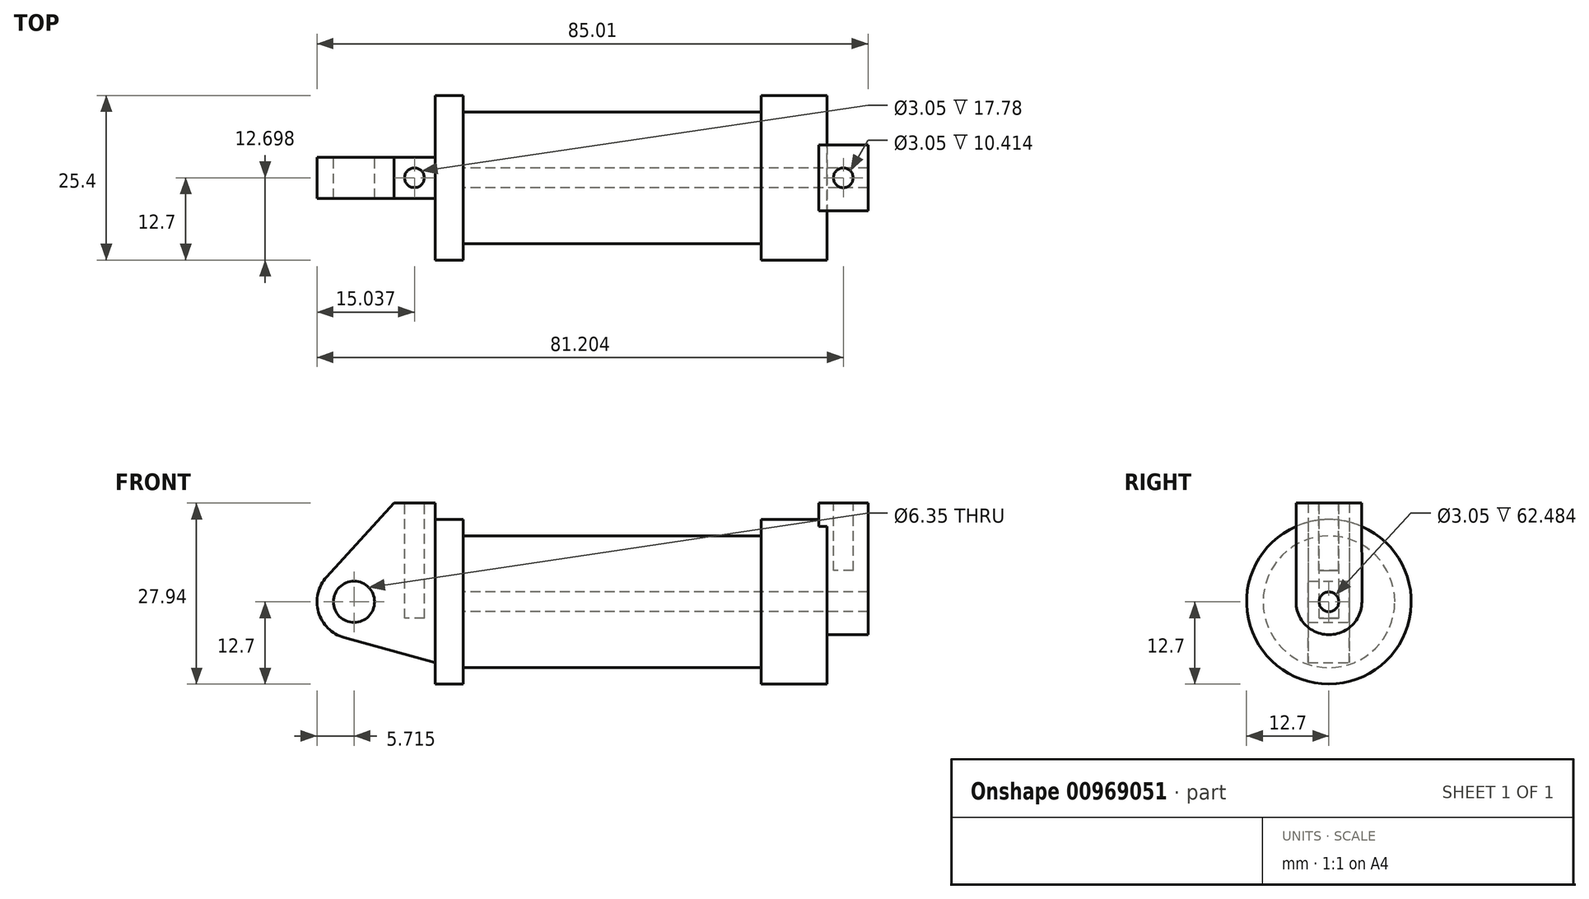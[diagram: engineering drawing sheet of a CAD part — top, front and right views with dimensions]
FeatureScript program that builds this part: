
annotation { "Feature Type Name" : "Feature", "Feature Type Description" : "" }
export const myFeature = defineFeature(function(context is Context, id is Id, definition is map)
    precondition{}
    {
        {
            var Q0;
            Q0=qCreatedBy(makeId("Front.planeOp"),FACE);
            var sketch = newSketch(context, id + "F0", { "sketchPlane" : qUnion([Q0])});
            skLineSegment(sketch, "E0", {"start": v(0, 0) * mm, "end": v(0, 12.7) * mm});
            skLineSegment(sketch, "E1", {"start": v(0, 12.7) * mm, "end": v(10.16, 12.7) * mm});
            skLineSegment(sketch, "E2", {"start": v(10.16, 12.7) * mm, "end": v(10.16, 10.16) * mm});
            skLineSegment(sketch, "E3", {"start": v(10.16, 10.16) * mm, "end": v(56.13, 10.16) * mm});
            skLineSegment(sketch, "E4", {"start": v(56.13, 10.16) * mm, "end": v(56.13, 12.7) * mm});
            skLineSegment(sketch, "E5", {"start": v(56.13, 12.7) * mm, "end": v(66.3, 12.7) * mm});
            skLineSegment(sketch, "E6", {"start": v(66.3, 12.7) * mm, "end": v(66.3, 0) * mm});
            skLineSegment(sketch, "E7", {"start": v(66.3, 0) * mm, "end": v(0, 0) * mm});
            skLineSegment(sketch, "E8", {"start": v(5.84, 15.24) * mm, "end": v(-0.5, 15.24) * mm});
            skLineSegment(sketch, "E9", {"start": v(-0.5, 15.24) * mm, "end": v(-10.88, 3.85) * mm});
            skLineSegment(sketch, "E10", {"start": v(0, 0) * mm, "end": v(-6.65, 0) * mm});
            skCircle(sketch, "E11", {"center": v(-6.65, 0) * mm, "radius": 5.72 * mm});
            skCircle(sketch, "E12", {"center": v(-6.65, 0) * mm, "radius": 3.18 * mm});
            skLineSegment(sketch, "E13", {"start": v(5.84, 15.24) * mm, "end": v(5.84, -9.4) * mm});
            skLineSegment(sketch, "E14", {"start": v(5.84, -9.4) * mm, "end": v(-8.18, -5.5) * mm});
            skSolve(sketch);
        }
        {
            var Q0;
            {var subQ0=sQuery(id+"F0.wireOp",EDGE,"E2");Q0=makeQuery(id+"F0.imprint","IMPRINT",FACE,{"disambiguationData":[TD([[makeQuery(id+"F0.imprint","IMPRINT",EDGE,{"derivedFrom":subQ0}),-1.0]])]});}
            var Q1;
            Q1=sQuery(id+"F0.wireOp",EDGE,"E10");
            revolve(context, id + "F1", {"surfaceOperationType" : NewSurfaceOperationType.NEW, "entities" : qUnion([Q0]), "axis" : qUnion([Q1]), "revolveType" : RevolveType.FULL});
        }
        {
            var Q0;
            {var subQ0=sQuery(id+"F0.wireOp",EDGE,"E14");Q0=makeQuery(id+"F0.imprint","IMPRINT",FACE,{"disambiguationData":[TD([[makeQuery(id+"F0.imprint","IMPRINT",EDGE,{"derivedFrom":subQ0}),-1.0]])]});}
            var Q1;
            {var subQ1=sQuery(id+"F0.wireOp",EDGE,"E0");Q1=makeQuery(id+"F0.imprint","IMPRINT",FACE,{"disambiguationData":[TD([[makeQuery(id+"F0.imprint","IMPRINT",EDGE,{"derivedFrom":subQ1}),1.0]])]});}
            var Q2;
            {var subQ5=sQuery(id+"F0.wireOp",EDGE,"E12");Q2=makeQuery(id+"F0.imprint","IMPRINT",FACE,{"disambiguationData":[TD([[makeQuery(id+"F0.imprint","IMPRINT",EDGE,{"derivedFrom":subQ5}),-1.0]])]});}
            var Q3;
            {var subQ0=sQuery(id+"F0.wireOp",EDGE,"E0");Q3=makeQuery(id+"F0.imprint","IMPRINT",FACE,{"disambiguationData":[TD([[makeQuery(id+"F0.imprint","IMPRINT",EDGE,{"derivedFrom":subQ0}),-1.0]])]});}
            extrude(context, id + "F2", {"entities" : qUnion([Q0, Q1, Q2, Q3]), "operationType" : NewBodyOperationType.ADD, "depth" : 3.17 * mm, "offsetDistance" : 25.4 * mm, "hasSecondDirection" : true, "secondDirectionOppositeDirection" : true, "secondDirectionDepth" : 3.17 * mm});
        }
        {
            var Q0;
            Q0=makeQuery(id+"F1.opRevolve","SWEPT_FACE",FACE,{"disambiguationData":[OSD([sQuery(id+"F0.wireOp",EDGE,"E6")])]});
            var sketch = newSketch(context, id + "F3", { "sketchPlane" : qUnion([Q0])});
            skCircle(sketch, "E15", {"center": v(0, 0) * mm, "radius": 1.52 * mm});
            skCircle(sketch, "E16", {"center": v(0, 0) * mm, "radius": 5.08 * mm});
            skLineSegment(sketch, "E17", {"start": v(-0.02, 15.24) * mm, "end": v(5.08, 15.24) * mm});
            skLineSegment(sketch, "E18", {"start": v(-0.02, 15.24) * mm, "end": v(-5.08, 15.24) * mm});
            skLineSegment(sketch, "E19", {"start": v(-5.08, 15.24) * mm, "end": v(-5.08, 0) * mm});
            skLineSegment(sketch, "E20", {"start": v(5.08, 15.24) * mm, "end": v(5.08, 0) * mm});
            skSolve(sketch);
        }
        {
            var Q0;
            {var subQ1=sQuery(id+"F3.wireOp",EDGE,"E17");Q0=makeQuery(id+"F3.imprint","IMPRINT",FACE,{"disambiguationData":[TD([[makeQuery(id+"F3.imprint","IMPRINT",EDGE,{"derivedFrom":subQ1}),-1.0]])]});}
            var Q1;
            {var subQ0=sQuery(id+"F3.wireOp",EDGE,"E19");var subQ1=sQuery(id+"F3.wireOp",EDGE,"E16");var subQ2=makeQuery(id+"F3.imprint","INTERSECT",VERTEX,{"derivedFrom":[subQ1,subQ0]});Q1=makeQuery(id+"F3.imprint","IMPRINT",FACE,{"disambiguationData":[TD([[makeQuery(id+"F3.imprint","IMPRINT",EDGE,{"disambiguationData":[TD([[subQ2,1.0]])],"derivedFrom":subQ1}),-1.0]])]});}
            var Q2;
            Q2=makeQuery(id+"F3.imprint","IMPRINT",FACE,{"disambiguationData":[TD([[makeQuery(id+"F3.imprint","IMPRINT",EDGE,{"derivedFrom":sQuery(id+"F3.wireOp",EDGE,"E15")}),-1.0]])]});
            extrude(context, id + "F4", {"entities" : qUnion([Q0, Q1, Q2]), "operationType" : NewBodyOperationType.ADD, "depth" : 6.35 * mm, "offsetDistance" : 25.4 * mm, "hasSecondDirection" : true, "secondDirectionOppositeDirection" : true, "secondDirectionDepth" : 1.27 * mm});
        }
        {
            var Q0;
            Q0=makeQuery(id+"F4.boolean.opBoolean","SPLIT",FACE,{"disambiguationData":[TD([makeQuery(id+"F4.opExtrude","SWEPT_FACE",FACE,{"disambiguationData":[OSD([sQuery(id+"F3.wireOp",EDGE,"E15")])]})])],"derivedFrom":makeQuery(id+"F1.opRevolve","SWEPT_FACE",FACE,{"disambiguationData":[OSD([sQuery(id+"F0.wireOp",EDGE,"E6")])]})});
            var Q1;
            Q1=makeQuery(id+"F1.opRevolve","SWEPT_FACE",FACE,{"disambiguationData":[OSD([sQuery(id+"F0.wireOp",EDGE,"E2")])]});
            extrude(context, id + "F5", {"entities" : qUnion([Q0]), "operationType" : NewBodyOperationType.REMOVE, "endBound" : BoundingType.UP_TO_SURFACE, "oppositeDirection" : true, "depth" : 25.4 * mm, "endBoundEntityFace" : qUnion([Q1]), "offsetDistance" : 25.4 * mm});
        }
        {
            var Q0;
            Q0=makeQuery(id+"F2.opExtrude","SWEPT_FACE",FACE,{"disambiguationData":[OSD([sQuery(id+"F0.wireOp",EDGE,"E8")])]});
            var sketch = newSketch(context, id + "F6", { "sketchPlane" : qUnion([Q0])});
            skCircle(sketch, "E21", {"center": v(2.67, 0) * mm, "radius": 1.52 * mm});
            skLineSegment(sketch, "E22", {"start": v(2.67, 3.18) * mm, "end": v(2.67, -3.18) * mm});
            skLineSegment(sketch, "E23", {"start": v(2.67, 3.18) * mm, "end": v(2.67, 0) * mm});
            skSolve(sketch);
        }
        {
            var Q0;
            Q0=makeQuery(id+"F4.opExtrude","SWEPT_FACE",FACE,{"disambiguationData":[OSD([sQuery(id+"F3.wireOp",EDGE,"E17"),sQuery(id+"F3.wireOp",EDGE,"E18")])]});
            var sketch = newSketch(context, id + "F7", { "sketchPlane" : qUnion([Q0])});
            skLineSegment(sketch, "E24", {"start": v(68.83, 5.08) * mm, "end": v(68.83, -5.08) * mm});
            skLineSegment(sketch, "E25", {"start": v(65.02, 0) * mm, "end": v(72.64, 0) * mm});
            skCircle(sketch, "E26", {"center": v(68.83, 0) * mm, "radius": 1.52 * mm});
            skSolve(sketch);
        }
        {
            var Q0;
            {var subQ0=sQuery(id+"F6.wireOp",EDGE,"E22");var subQ1=sQuery(id+"F6.wireOp",EDGE,"E21");var subQ2=makeQuery(id+"F6.imprint","INTERSECT",VERTEX,{"derivedFrom":[subQ1,subQ0]});Q0=makeQuery(id+"F6.imprint","IMPRINT",FACE,{"disambiguationData":[TD([[makeQuery(id+"F6.imprint","IMPRINT",EDGE,{"disambiguationData":[TD([[subQ2,1.0]])],"derivedFrom":subQ1}),1.0]])]});}
            var Q1;
            {var subQ0=sQuery(id+"F6.wireOp",EDGE,"E22");var subQ1=sQuery(id+"F6.wireOp",EDGE,"E21");var subQ2=makeQuery(id+"F6.imprint","INTERSECT",VERTEX,{"derivedFrom":[subQ1,subQ0]});Q1=makeQuery(id+"F6.imprint","IMPRINT",FACE,{"disambiguationData":[TD([[makeQuery(id+"F6.imprint","IMPRINT",EDGE,{"disambiguationData":[TD([[subQ2,-1.0]])],"derivedFrom":subQ1}),1.0]])]});}
            extrude(context, id + "F8", {"entities" : qUnion([Q0, Q1]), "operationType" : NewBodyOperationType.REMOVE, "oppositeDirection" : true, "depth" : 17.78 * mm, "offsetDistance" : 25.4 * mm});
        }
        {
            var Q0;
            {var subQ0=sQuery(id+"F7.wireOp",EDGE,"E26");var subQ1=sQuery(id+"F7.wireOp",EDGE,"E24");var subQ2=makeQuery(id+"F7.imprint","INTERSECT",VERTEX,{"disambiguationData":[OD(0.0)],"derivedFrom":[subQ1,subQ0]});Q0=makeQuery(id+"F7.imprint","IMPRINT",FACE,{"disambiguationData":[TD([[makeQuery(id+"F7.imprint","IMPRINT",EDGE,{"disambiguationData":[TD([[subQ2,-1.0]])],"derivedFrom":subQ1}),-1.0]])]});}
            var Q1;
            {var subQ0=sQuery(id+"F7.wireOp",EDGE,"E26");var subQ1=sQuery(id+"F7.wireOp",EDGE,"E24");var subQ2=makeQuery(id+"F7.imprint","INTERSECT",VERTEX,{"disambiguationData":[OD(0.0)],"derivedFrom":[subQ1,subQ0]});Q1=makeQuery(id+"F7.imprint","IMPRINT",FACE,{"disambiguationData":[TD([[makeQuery(id+"F7.imprint","IMPRINT",EDGE,{"disambiguationData":[TD([[subQ2,-1.0]])],"derivedFrom":subQ1}),1.0]])]});}
            var Q2;
            {var subQ0=sQuery(id+"F7.wireOp",EDGE,"E25");var subQ1=sQuery(id+"F7.wireOp",EDGE,"E24");var subQ2=makeQuery(id+"F7.imprint","INTERSECT",VERTEX,{"derivedFrom":[subQ1,subQ0]});Q2=makeQuery(id+"F7.imprint","IMPRINT",FACE,{"disambiguationData":[TD([[makeQuery(id+"F7.imprint","IMPRINT",EDGE,{"disambiguationData":[TD([[subQ2,-1.0]])],"derivedFrom":subQ1}),-1.0]])]});}
            var Q3;
            {var subQ0=sQuery(id+"F7.wireOp",EDGE,"E25");var subQ1=sQuery(id+"F7.wireOp",EDGE,"E24");var subQ2=makeQuery(id+"F7.imprint","INTERSECT",VERTEX,{"derivedFrom":[subQ1,subQ0]});Q3=makeQuery(id+"F7.imprint","IMPRINT",FACE,{"disambiguationData":[TD([[makeQuery(id+"F7.imprint","IMPRINT",EDGE,{"disambiguationData":[TD([[subQ2,-1.0]])],"derivedFrom":subQ1}),1.0]])]});}
            extrude(context, id + "F9", {"entities" : qUnion([Q0, Q1, Q2, Q3]), "operationType" : NewBodyOperationType.REMOVE, "oppositeDirection" : true, "depth" : 10.4 * mm, "offsetDistance" : 25.4 * mm});
        }
    });
